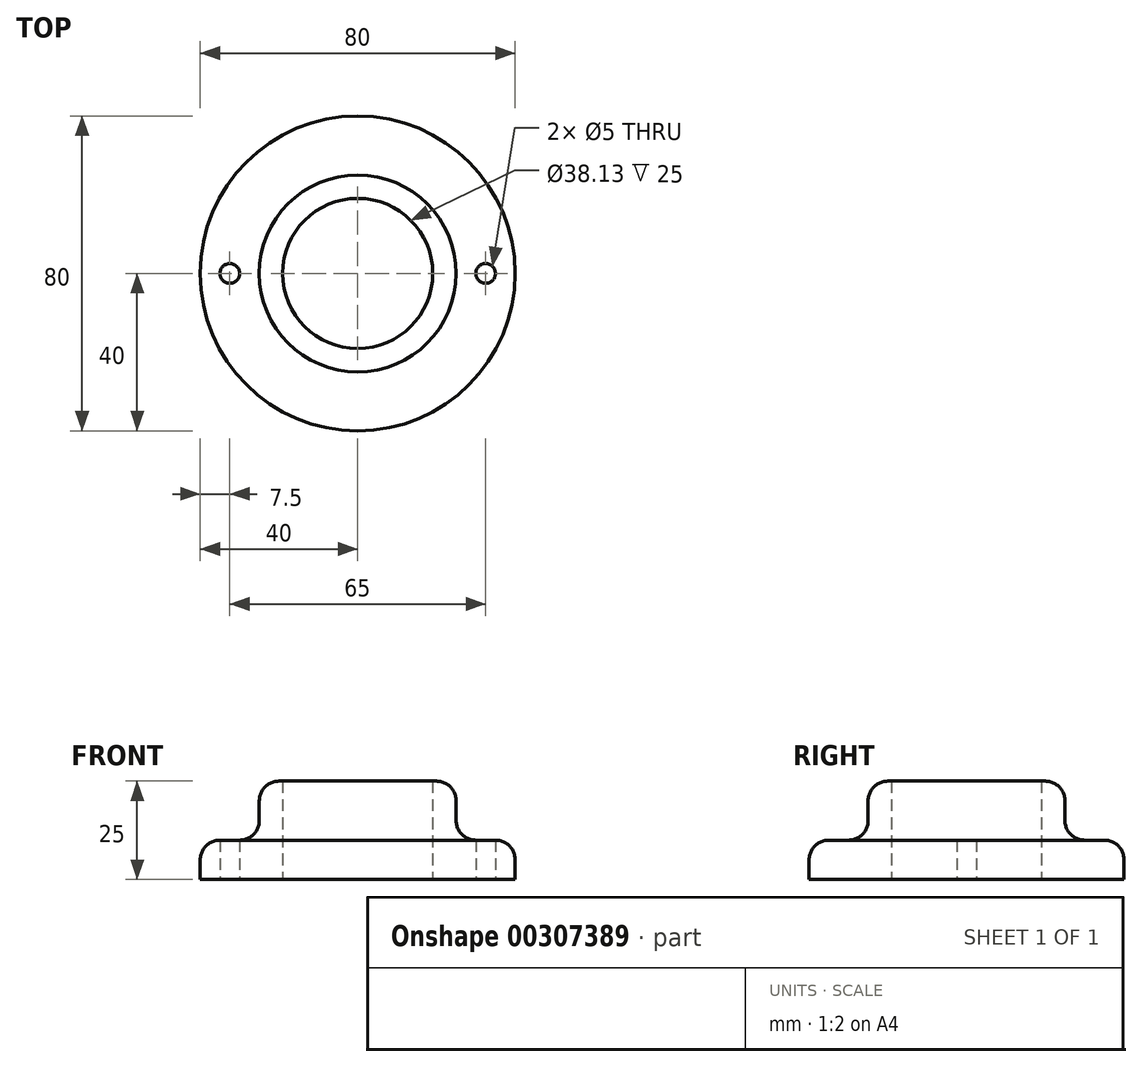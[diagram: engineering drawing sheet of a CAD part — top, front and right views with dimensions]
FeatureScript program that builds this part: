
annotation { "Feature Type Name" : "Feature", "Feature Type Description" : "" }
export const myFeature = defineFeature(function(context is Context, id is Id, definition is map)
    precondition{}
    {
        {
            var Q0;
            Q0=qCreatedBy(makeId("Top.planeOp"),FACE);
            var sketch = newSketch(context, id + "F0", { "sketchPlane" : qUnion([Q0])});
            skCircle(sketch, "E0", {"center": v(0, 0) * mm, "radius": 40 * mm});
            skCircle(sketch, "E1", {"center": v(0, 0) * mm, "radius": 25 * mm});
            skLineSegment(sketch, "E2", {"start": v(-40, 0) * mm, "end": v(40, 0) * mm, "construction": true});
            skCircle(sketch, "E3", {"center": v(0, 0) * mm, "radius": 32.5 * mm, "construction": true});
            skCircle(sketch, "E4", {"center": v(32.5, 0) * mm, "radius": 2.5 * mm});
            skCircle(sketch, "E5", {"center": v(-32.5, 0) * mm, "radius": 2.5 * mm});
            skLineSegment(sketch, "E6", {"start": v(0, -32.5) * mm, "end": v(0, -40) * mm, "construction": true});
            skCircle(sketch, "E7", {"center": v(0, 0) * mm, "radius": 19.07 * mm});
            skSolve(sketch);
        }
        {
            var Q0;
            Q0=makeQuery(id+"F0.imprint","IMPRINT",FACE,{"disambiguationData":[TD([[makeQuery(id+"F0.imprint","IMPRINT",EDGE,{"derivedFrom":sQuery(id+"F0.wireOp",EDGE,"E1")}),1.0]])]});
            extrude(context, id + "F1", {"entities" : qUnion([Q0]), "depth" : 25 * mm});
        }
        {
            var Q0;
            Q0=makeQuery(id+"F0.imprint","IMPRINT",FACE,{"disambiguationData":[TD([[makeQuery(id+"F0.imprint","IMPRINT",EDGE,{"derivedFrom":sQuery(id+"F0.wireOp",EDGE,"E0")}),1.0]])]});
            extrude(context, id + "F2", {"entities" : qUnion([Q0]), "operationType" : NewBodyOperationType.ADD, "depth" : 10 * mm});
        }
        {
            var Q0;
            Q0=makeQuery(id+"F2.opExtrude","CAP_EDGE",EDGE,{"disambiguationData":[OSD([sQuery(id+"F0.wireOp",EDGE,"E0")])],"isStart":false});
            var Q1;
            Q1=makeQuery(id+"F1.opExtrude","CAP_EDGE",EDGE,{"disambiguationData":[OSD([sQuery(id+"F0.wireOp",EDGE,"E1")])],"isStart":false});
            fillet(context, id + "F3", {"entities" : qUnion([Q0, Q1]), "radius" : 5 * mm, "tangentPropagation" : true, "allowEdgeOverflow" : false});
        }
        {
            var Q0;
            Q0=makeQuery(id+"F1.opExtrude","SWEPT_FACE",FACE,{"disambiguationData":[OSD([sQuery(id+"F0.wireOp",EDGE,"E1")])]});
            fillet(context, id + "F4", {"entities" : qUnion([Q0]), "radius" : 5 * mm, "tangentPropagation" : true, "allowEdgeOverflow" : false});
        }
    });
